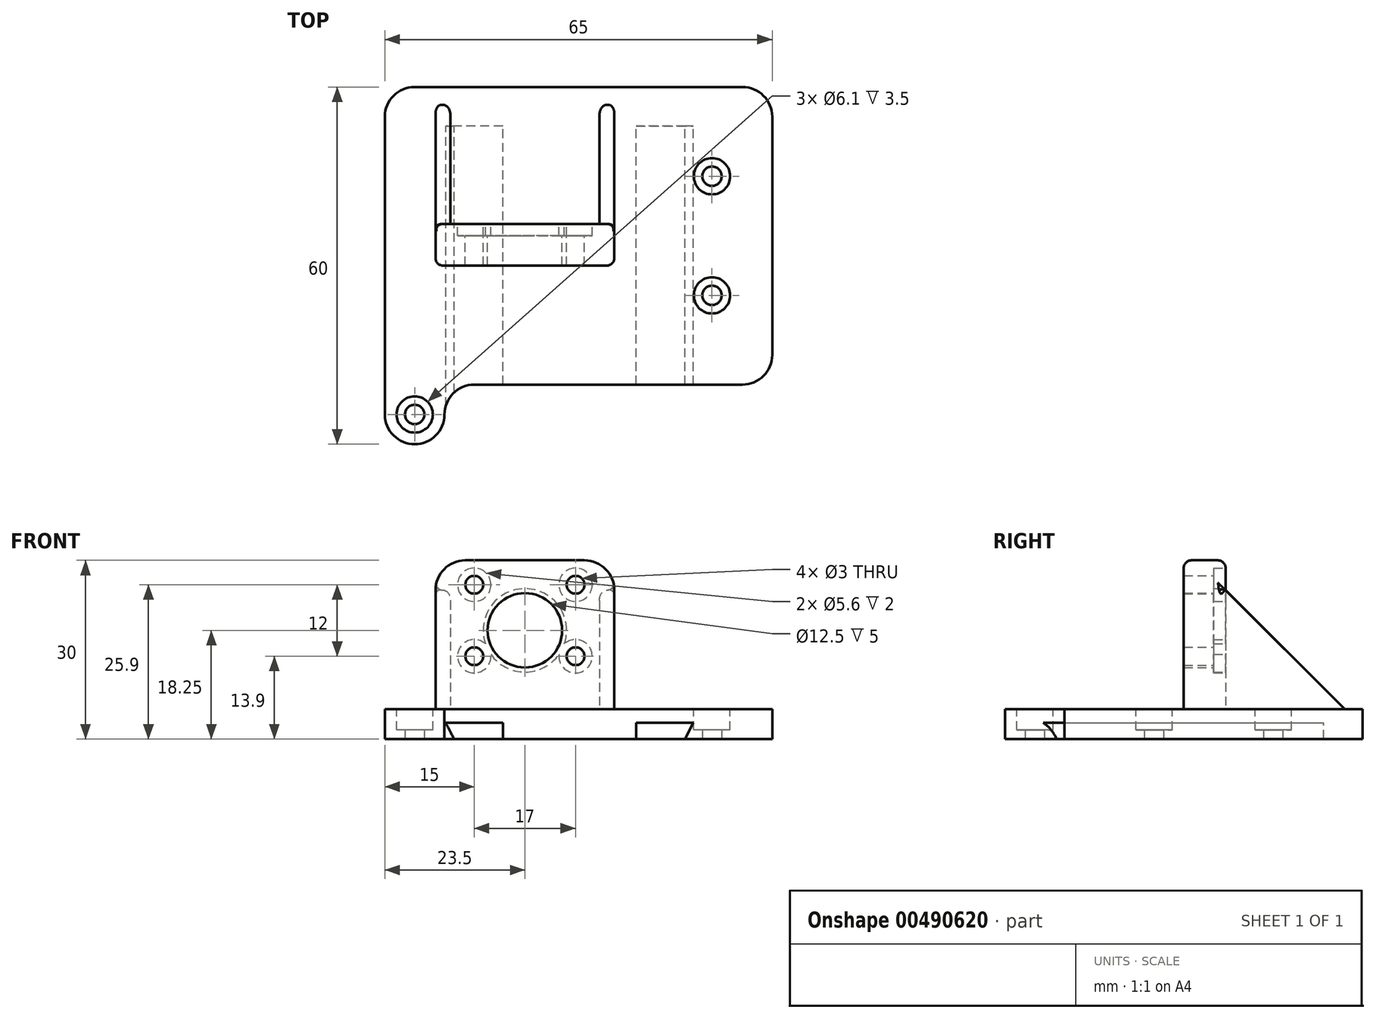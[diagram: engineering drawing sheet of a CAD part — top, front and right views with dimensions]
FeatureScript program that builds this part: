
annotation { "Feature Type Name" : "Feature", "Feature Type Description" : "" }
export const myFeature = defineFeature(function(context is Context, id is Id, definition is map)
    precondition{}
    {
        {
            var Q0;
            Q0=qCreatedBy(makeId("Top.planeOp"),FACE);
            var sketch = newSketch(context, id + "F0", { "sketchPlane" : qUnion([Q0])});
            skLineSegment(sketch, "E0", {"start": v(-32.5, 25) * mm, "end": v(22.5, 25) * mm});
            skLineSegment(sketch, "E1", {"start": v(27.5, 20) * mm, "end": v(27.5, -20) * mm});
            skLineSegment(sketch, "E2", {"start": v(22.5, -25) * mm, "end": v(-22.5, -25) * mm});
            skLineSegment(sketch, "E3", {"start": v(-27.5, -30) * mm, "end": v(-27.5, -30) * mm});
            skLineSegment(sketch, "E4", {"start": v(-32.5, -35) * mm, "end": v(-32.5, -35) * mm});
            skLineSegment(sketch, "E5", {"start": v(-37.5, -30) * mm, "end": v(-37.5, 20) * mm});
            skPoint(sketch, "E6.visualSharp", {"position": v(27.5, 25) * mm});
            skArc(sketch, "E6.filletArc", {"start": v(27.5, 20) * mm, "mid": v(26.04, 23.54) * mm, "end": v(22.5, 25) * mm});
            skPoint(sketch, "E7.visualSharp", {"position": v(27.5, -25) * mm});
            skArc(sketch, "E7.filletArc", {"start": v(22.5, -25) * mm, "mid": v(26.04, -23.54) * mm, "end": v(27.5, -20) * mm});
            skPoint(sketch, "E8.visualSharp", {"position": v(-27.5, -25) * mm});
            skArc(sketch, "E8.filletArc", {"start": v(-22.5, -25) * mm, "mid": v(-26.04, -26.46) * mm, "end": v(-27.5, -30) * mm});
            skPoint(sketch, "E9.visualSharp", {"position": v(-27.5, -35) * mm});
            skArc(sketch, "E9.filletArc", {"start": v(-32.5, -35) * mm, "mid": v(-28.96, -33.54) * mm, "end": v(-27.5, -30) * mm});
            skPoint(sketch, "E10.visualSharp", {"position": v(-37.5, -35) * mm});
            skArc(sketch, "E10.filletArc", {"start": v(-37.5, -30) * mm, "mid": v(-36.04, -33.54) * mm, "end": v(-32.5, -35) * mm});
            skCircle(sketch, "E11", {"center": v(-32.5, -30) * mm, "radius": 1.63 * mm});
            skCircle(sketch, "E12", {"center": v(17.4, 10) * mm, "radius": 1.63 * mm});
            skCircle(sketch, "E13", {"center": v(17.4, -10) * mm, "radius": 1.63 * mm});
            skPoint(sketch, "E14.visualSharp", {"position": v(-37.5, 25) * mm});
            skArc(sketch, "E14.filletArc", {"start": v(-32.5, 25) * mm, "mid": v(-36.04, 23.54) * mm, "end": v(-37.5, 20) * mm});
            skSolve(sketch);
        }
        {
            var Q0;
            Q0=makeQuery(id+"F0.imprint","IMPRINT",FACE,{"disambiguationData":[TD([[makeQuery(id+"F0.imprint","IMPRINT",EDGE,{"derivedFrom":sQuery(id+"F0.wireOp",EDGE,"E0")}),-1.0]])]});
            extrude(context, id + "F1", {"entities" : qUnion([Q0]), "depth" : 5 * mm});
        }
        {
            var Q0;
            Q0=makeQuery(id+"F1.opExtrude","CAP_FACE",FACE,{"disambiguationData":[OSD([sQuery(id+"F0.wireOp",EDGE,"E0"),sQuery(id+"F0.wireOp",EDGE,"E1"),sQuery(id+"F0.wireOp",EDGE,"E2"),sQuery(id+"F0.wireOp",EDGE,"E5"),sQuery(id+"F0.wireOp",EDGE,"E6.filletArc"),sQuery(id+"F0.wireOp",EDGE,"E7.filletArc"),sQuery(id+"F0.wireOp",EDGE,"E8.filletArc"),sQuery(id+"F0.wireOp",EDGE,"E9.filletArc"),sQuery(id+"F0.wireOp",EDGE,"E10.filletArc"),sQuery(id+"F0.wireOp",EDGE,"nNRTAZ3m-UcFT-XEbX-bW4l-1CdXOK1OszjN"),sQuery(id+"F0.wireOp",EDGE,"OskZh1Qr-N4c8-G8Yp-psBz-cHskyBAqI7m4"),sQuery(id+"F0.wireOp",EDGE,"E11")])],"isStart":false});
            var sketch = newSketch(context, id + "F2", { "sketchPlane" : qUnion([Q0])});
            skCircle(sketch, "E15", {"center": v(-32.5, -30) * mm, "radius": 3.05 * mm});
            skCircle(sketch, "E16", {"center": v(17.4, 10) * mm, "radius": 3.05 * mm});
            skCircle(sketch, "E17", {"center": v(17.4, -10) * mm, "radius": 3.05 * mm});
            skSolve(sketch);
        }
        {
            var Q0;
            Q0=makeQuery(id+"F2.imprint","IMPRINT",FACE,{"disambiguationData":[TD([[makeQuery(id+"F2.imprint","IMPRINT",EDGE,{"derivedFrom":sQuery(id+"F2.wireOp",EDGE,"E16")}),1.0]])]});
            var Q1;
            Q1=makeQuery(id+"F2.imprint","IMPRINT",FACE,{"disambiguationData":[TD([[makeQuery(id+"F2.imprint","IMPRINT",EDGE,{"derivedFrom":sQuery(id+"F2.wireOp",EDGE,"E17")}),1.0]])]});
            var Q2;
            Q2=makeQuery(id+"F2.imprint","IMPRINT",FACE,{"disambiguationData":[TD([[makeQuery(id+"F2.imprint","IMPRINT",EDGE,{"derivedFrom":sQuery(id+"F2.wireOp",EDGE,"E15")}),1.0]])]});
            extrude(context, id + "F3", {"entities" : qUnion([Q0, Q1, Q2]), "operationType" : NewBodyOperationType.REMOVE, "oppositeDirection" : true, "depth" : 3.5 * mm});
        }
        {
            var Q0;
            Q0=makeQuery(id+"F1.opExtrude","CAP_FACE",FACE,{"disambiguationData":[OSD([sQuery(id+"F0.wireOp",EDGE,"E0"),sQuery(id+"F0.wireOp",EDGE,"E1"),sQuery(id+"F0.wireOp",EDGE,"E2"),sQuery(id+"F0.wireOp",EDGE,"E5"),sQuery(id+"F0.wireOp",EDGE,"E6.filletArc"),sQuery(id+"F0.wireOp",EDGE,"E7.filletArc"),sQuery(id+"F0.wireOp",EDGE,"E8.filletArc"),sQuery(id+"F0.wireOp",EDGE,"E9.filletArc"),sQuery(id+"F0.wireOp",EDGE,"E10.filletArc"),sQuery(id+"F0.wireOp",EDGE,"nNRTAZ3m-UcFT-XEbX-bW4l-1CdXOK1OszjN"),sQuery(id+"F0.wireOp",EDGE,"OskZh1Qr-N4c8-G8Yp-psBz-cHskyBAqI7m4"),sQuery(id+"F0.wireOp",EDGE,"E11")])],"isStart":false});
            var sketch = newSketch(context, id + "F4", { "sketchPlane" : qUnion([Q0])});
            skLineSegment(sketch, "E18.bottom", {"start": v(-29, 2) * mm, "end": v(1, 2) * mm});
            skLineSegment(sketch, "E18.top", {"start": v(-29, -5) * mm, "end": v(1, -5) * mm});
            skLineSegment(sketch, "E18.left", {"start": v(-29, 2) * mm, "end": v(-29, -5) * mm});
            skLineSegment(sketch, "E18.right", {"start": v(1, 2) * mm, "end": v(1, -5) * mm});
            skSolve(sketch);
        }
        {
            var Q0;
            Q0=makeQuery(id+"F4.imprint","IMPRINT",FACE,{"disambiguationData":[TD([[makeQuery(id+"F4.imprint","IMPRINT",EDGE,{"derivedFrom":sQuery(id+"F4.wireOp",EDGE,"E18.bottom")}),-1.0]])]});
            extrude(context, id + "F5", {"entities" : qUnion([Q0]), "operationType" : NewBodyOperationType.ADD, "depth" : 25 * mm});
        }
        {
            var Q0;
            Q0=makeQuery(id+"F5.opExtrude","CAP_EDGE",EDGE,{"disambiguationData":[OSD([sQuery(id+"F4.wireOp",EDGE,"E18.left")])],"isStart":false});
            var Q1;
            Q1=makeQuery(id+"F5.opExtrude","CAP_EDGE",EDGE,{"disambiguationData":[OSD([sQuery(id+"F4.wireOp",EDGE,"E18.right")])],"isStart":false});
            fillet(context, id + "F6", {"entities" : qUnion([Q0, Q1]), "radius" : 5 * mm, "tangentPropagation" : true, "allowEdgeOverflow" : false});
        }
        {
            var Q0;
            Q0=makeQuery(id+"F5.opExtrude","SWEPT_FACE",FACE,{"disambiguationData":[OSD([sQuery(id+"F4.wireOp",EDGE,"E18.right")])]});
            var sketch = newSketch(context, id + "F7", { "sketchPlane" : qUnion([Q0])});
            skLineSegment(sketch, "E19", {"start": v(2, 25) * mm, "end": v(2, 5) * mm});
            skLineSegment(sketch, "E20", {"start": v(2, 5) * mm, "end": v(22, 5) * mm});
            skLineSegment(sketch, "E21", {"start": v(22, 5) * mm, "end": v(2, 25) * mm});
            skSolve(sketch);
        }
        {
            var Q0;
            Q0=makeQuery(id+"F5.opExtrude","SWEPT_FACE",FACE,{"disambiguationData":[OSD([sQuery(id+"F4.wireOp",EDGE,"E18.left")])]});
            var sketch = newSketch(context, id + "F8", { "sketchPlane" : qUnion([Q0])});
            skLineSegment(sketch, "E22", {"start": v(-2, 25) * mm, "end": v(-2, 5) * mm});
            skLineSegment(sketch, "E23", {"start": v(-2, 5) * mm, "end": v(-22, 5) * mm});
            skLineSegment(sketch, "E24", {"start": v(-22, 5) * mm, "end": v(-2, 25) * mm});
            skSolve(sketch);
        }
        {
            var Q0;
            Q0=makeQuery(id+"F7.imprint","IMPRINT",FACE,{"disambiguationData":[TD([[makeQuery(id+"F7.imprint","IMPRINT",EDGE,{"derivedFrom":sQuery(id+"F7.wireOp",EDGE,"E19")}),1.0]])]});
            extrude(context, id + "F9", {"entities" : qUnion([Q0]), "operationType" : NewBodyOperationType.ADD, "oppositeDirection" : true, "depth" : 2.5 * mm});
        }
        {
            var Q0;
            Q0=makeQuery(id+"F8.imprint","IMPRINT",FACE,{"disambiguationData":[TD([[makeQuery(id+"F8.imprint","IMPRINT",EDGE,{"derivedFrom":sQuery(id+"F8.wireOp",EDGE,"E22")}),-1.0]])]});
            extrude(context, id + "F10", {"entities" : qUnion([Q0]), "operationType" : NewBodyOperationType.ADD, "oppositeDirection" : true, "depth" : 2.5 * mm});
        }
        {
            var Q0;
            Q0=makeQuery(id+"F5.opExtrude","CAP_EDGE",EDGE,{"disambiguationData":[OSD([sQuery(id+"F4.wireOp",EDGE,"E18.bottom")])],"isStart":false});
            var Q1;
            Q1=makeQuery(id+"F10.opExtrude","CAP_EDGE",EDGE,{"disambiguationData":[OSD([sQuery(id+"F8.wireOp",EDGE,"E24")])],"isStart":false});
            var Q2;
            Q2=makeQuery(id+"F9.opExtrude","CAP_EDGE",EDGE,{"disambiguationData":[OSD([sQuery(id+"F7.wireOp",EDGE,"E21")])],"isStart":false});
            var Q3;
            Q3=makeQuery(id+"F5.opExtrude","SWEPT_EDGE",EDGE,{"disambiguationData":[OSD([sQuery(id+"F4.wireOp",EDGE,"E18.top"),sQuery(id+"F4.wireOp",EDGE,"E18.left")])]});
            fillet(context, id + "F11", {"entities" : qUnion([Q0, Q1, Q2, Q3]), "radius" : 1.25 * mm, "tangentPropagation" : true, "allowEdgeOverflow" : false});
        }
        {
            var Q0;
            Q0=makeQuery(id+"F10.opExtrude","CAP_EDGE",EDGE,{"disambiguationData":[OSD([sQuery(id+"F8.wireOp",EDGE,"E24")])],"isStart":true});
            var Q1;
            Q1=makeQuery(id+"F9.opExtrude","CAP_EDGE",EDGE,{"disambiguationData":[OSD([sQuery(id+"F7.wireOp",EDGE,"E21")])],"isStart":true});
            fillet(context, id + "F12", {"entities" : qUnion([Q0, Q1]), "radius" : 1 * mm, "tangentPropagation" : true, "allowEdgeOverflow" : false});
        }
        {
            var Q0;
            Q0=makeQuery(id+"F5.opExtrude","SWEPT_FACE",FACE,{"disambiguationData":[OSD([sQuery(id+"F4.wireOp",EDGE,"E18.bottom")])]});
            var sketch = newSketch(context, id + "F13", { "sketchPlane" : qUnion([Q0])});
            skCircle(sketch, "E25", {"center": v(14, 18.25) * mm, "radius": 6.25 * mm});
            skCircle(sketch, "E26", {"center": v(5.5, 25.9) * mm, "radius": 1.5 * mm});
            skCircle(sketch, "E27", {"center": v(22.5, 13.9) * mm, "radius": 1.5 * mm});
            skCircle(sketch, "E28", {"center": v(22.5, 25.9) * mm, "radius": 1.5 * mm});
            skCircle(sketch, "E29", {"center": v(5.5, 13.9) * mm, "radius": 1.5 * mm});
            skSolve(sketch);
        }
        {
            var Q0;
            Q0=makeQuery(id+"F13.imprint","IMPRINT",FACE,{"disambiguationData":[TD([[makeQuery(id+"F13.imprint","IMPRINT",EDGE,{"derivedFrom":sQuery(id+"F13.wireOp",EDGE,"E26")}),1.0]])]});
            var Q1;
            Q1=makeQuery(id+"F13.imprint","IMPRINT",FACE,{"disambiguationData":[TD([[makeQuery(id+"F13.imprint","IMPRINT",EDGE,{"derivedFrom":sQuery(id+"F13.wireOp",EDGE,"E29")}),1.0]])]});
            var Q2;
            Q2=makeQuery(id+"F13.imprint","IMPRINT",FACE,{"disambiguationData":[TD([[makeQuery(id+"F13.imprint","IMPRINT",EDGE,{"derivedFrom":sQuery(id+"F13.wireOp",EDGE,"E25")}),1.0]])]});
            var Q3;
            Q3=makeQuery(id+"F13.imprint","IMPRINT",FACE,{"disambiguationData":[TD([[makeQuery(id+"F13.imprint","IMPRINT",EDGE,{"derivedFrom":sQuery(id+"F13.wireOp",EDGE,"E28")}),1.0]])]});
            var Q4;
            Q4=makeQuery(id+"F13.imprint","IMPRINT",FACE,{"disambiguationData":[TD([[makeQuery(id+"F13.imprint","IMPRINT",EDGE,{"derivedFrom":sQuery(id+"F13.wireOp",EDGE,"E27")}),1.0]])]});
            extrude(context, id + "F14", {"entities" : qUnion([Q0, Q1, Q2, Q3, Q4]), "operationType" : NewBodyOperationType.REMOVE, "oppositeDirection" : true, "depth" : 25.4 * mm});
        }
        {
            var Q0;
            Q0=makeQuery(id+"F5.opExtrude","SWEPT_FACE",FACE,{"disambiguationData":[OSD([sQuery(id+"F4.wireOp",EDGE,"E18.bottom")])]});
            var sketch = newSketch(context, id + "F15", { "sketchPlane" : qUnion([Q0])});
            skCircle(sketch, "E30", {"center": v(5.5, 25.9) * mm, "radius": 2.8 * mm});
            skArc(sketch, "E31", {"start": v(7.38, 15.97) * mm, "mid": v(3, 12.62) * mm, "end": v(8.28, 14.21) * mm});
            skArc(sketch, "E32", {"start": v(19.72, 14.21) * mm, "mid": v(25, 12.62) * mm, "end": v(20.62, 15.97) * mm});
            skCircle(sketch, "E33", {"center": v(22.5, 25.9) * mm, "radius": 2.8 * mm});
            skArc(sketch, "E34", {"start": v(8.28, 14.21) * mm, "mid": v(14, 11.25) * mm, "end": v(19.72, 14.21) * mm});
            skArc(sketch, "E35.trimOffspring", {"start": v(20.62, 15.97) * mm, "mid": v(14, 25.25) * mm, "end": v(7.38, 15.97) * mm});
            skSolve(sketch);
        }
        {
            var Q0;
            Q0=makeQuery(id+"F15.imprint","IMPRINT",FACE,{"disambiguationData":[TD([[makeQuery(id+"F15.imprint","IMPRINT",EDGE,{"derivedFrom":sQuery(id+"F15.wireOp",EDGE,"E31")}),1.0]])]});
            var Q1;
            Q1=makeQuery(id+"F15.imprint","IMPRINT",FACE,{"disambiguationData":[TD([[makeQuery(id+"F15.imprint","IMPRINT",EDGE,{"derivedFrom":sQuery(id+"F15.wireOp",EDGE,"E30")}),1.0]])]});
            var Q2;
            Q2=makeQuery(id+"F15.imprint","IMPRINT",FACE,{"disambiguationData":[TD([[makeQuery(id+"F15.imprint","IMPRINT",EDGE,{"derivedFrom":sQuery(id+"F15.wireOp",EDGE,"E33")}),1.0]])]});
            extrude(context, id + "F16", {"entities" : qUnion([Q0, Q1, Q2]), "operationType" : NewBodyOperationType.REMOVE, "oppositeDirection" : true, "depth" : 2 * mm});
        }
        {
            var Q0;
            Q0=makeQuery(id+"F1.opExtrude","SWEPT_FACE",FACE,{"disambiguationData":[OSD([sQuery(id+"F0.wireOp",EDGE,"E2")])]});
            var sketch = newSketch(context, id + "F17", { "sketchPlane" : qUnion([Q0])});
            skLineSegment(sketch, "E36", {"start": v(4.7, 0) * mm, "end": v(4.7, 2.7) * mm});
            skLineSegment(sketch, "E37", {"start": v(4.7, 2.7) * mm, "end": v(14.29, 2.7) * mm});
            skLineSegment(sketch, "E38", {"start": v(14.29, 2.71) * mm, "end": v(12.88, 0) * mm});
            skLineSegment(sketch, "E39", {"start": v(12.88, 0) * mm, "end": v(4.7, 0) * mm});
            skLineSegment(sketch, "E40", {"start": v(-17.71, 0) * mm, "end": v(-17.71, 2.71) * mm});
            skLineSegment(sketch, "E41", {"start": v(-17.71, 2.71) * mm, "end": v(-27.3, 2.7) * mm});
            skLineSegment(sketch, "E42", {"start": v(-27.3, 2.71) * mm, "end": v(-25.9, 0) * mm});
            skLineSegment(sketch, "E43", {"start": v(-25.9, 0) * mm, "end": v(-17.71, 0) * mm});
            skSolve(sketch);
        }
        {
            var Q0;
            {var subQ0=sQuery(id+"F17.wireOp",EDGE,"E40");Q0=makeQuery(id+"F17.imprint","IMPRINT",FACE,{"disambiguationData":[TD([[makeQuery(id+"F17.imprint","IMPRINT",EDGE,{"derivedFrom":subQ0}),1.0]])]});}
            var Q1;
            Q1=makeQuery(id+"F17.imprint","IMPRINT",FACE,{"disambiguationData":[TD([[makeQuery(id+"F17.imprint","IMPRINT",EDGE,{"derivedFrom":sQuery(id+"F17.wireOp",EDGE,"E36")}),-1.0]])]});
            var Q2;
            {var subQ0=sQuery(id+"F17.wireOp",EDGE,"E42");Q2=makeQuery(id+"F17.imprint","IMPRINT",FACE,{"disambiguationData":[TD([[makeQuery(id+"F17.imprint","IMPRINT",EDGE,{"derivedFrom":subQ0}),1.0]])]});}
            extrude(context, id + "F18", {"entities" : qUnion([Q0, Q1, Q2]), "operationType" : NewBodyOperationType.REMOVE, "endBound" : BoundingType.SYMMETRIC, "depth" : 86.9 * mm});
        }
    });
